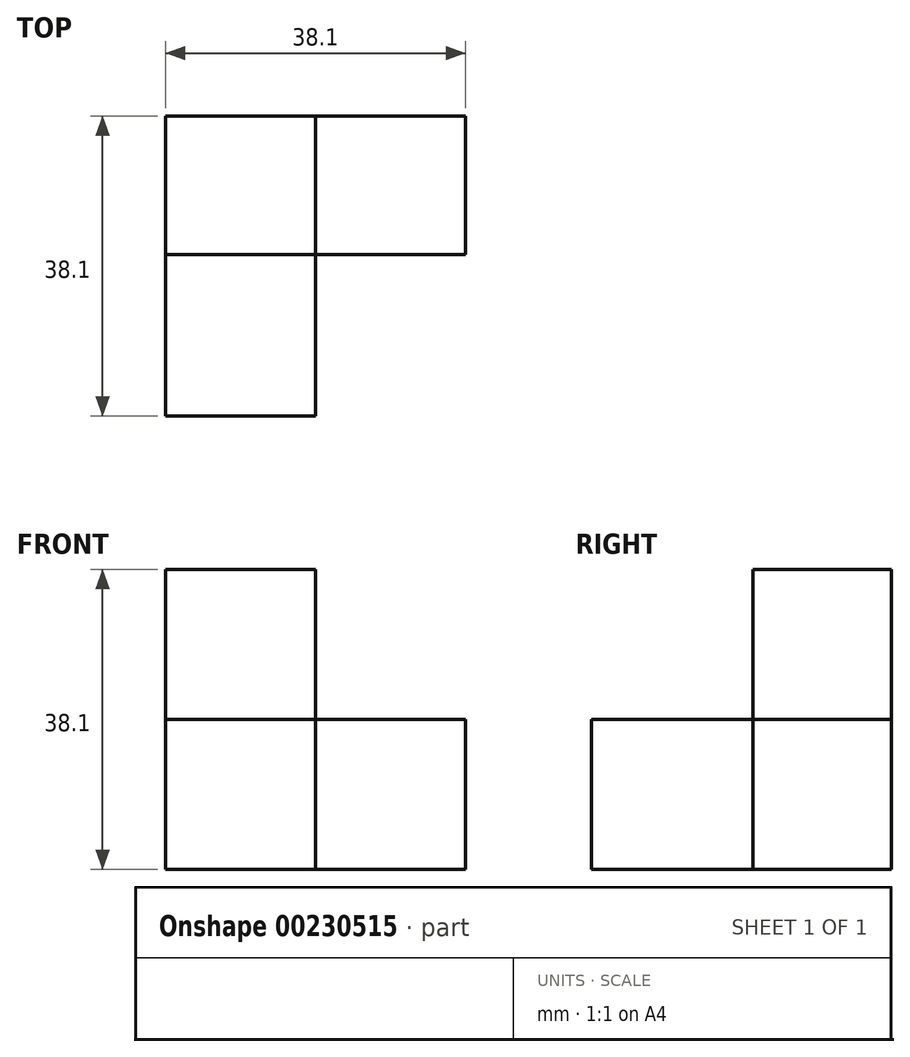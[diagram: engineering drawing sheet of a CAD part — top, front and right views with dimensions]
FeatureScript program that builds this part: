
annotation { "Feature Type Name" : "Feature", "Feature Type Description" : "" }
export const myFeature = defineFeature(function(context is Context, id is Id, definition is map)
    precondition{}
    {
        {
            var Q0;
            Q0=qCreatedBy(makeId("Top.planeOp"),FACE);
            var sketch = newSketch(context, id + "F0", { "sketchPlane" : qUnion([Q0])});
            skLineSegment(sketch, "E0.bottom", {"start": v(-44.26, -20.52) * mm, "end": v(-25.2, -20.52) * mm});
            skLineSegment(sketch, "E0.top", {"start": v(-44.26, 17.58) * mm, "end": v(-25.2, 17.58) * mm});
            skLineSegment(sketch, "E0.left", {"start": v(-44.26, -20.52) * mm, "end": v(-44.26, 17.58) * mm});
            skLineSegment(sketch, "E0.right", {"start": v(-25.2, -20.52) * mm, "end": v(-25.2, 17.58) * mm});
            skSolve(sketch);
        }
        {
            var Q0;
            Q0=makeQuery(id+"F0.imprint","IMPRINT",FACE,{"disambiguationData":[TD([[makeQuery(id+"F0.imprint","IMPRINT",EDGE,{"derivedFrom":sQuery(id+"F0.wireOp",EDGE,"E0.bottom")}),1.0]])]});
            extrude(context, id + "F1", {"entities" : qUnion([Q0]), "depth" : 19.05 * mm});
        }
        {
            var Q0;
            Q0=makeQuery(id+"F1.opExtrude","SWEPT_FACE",FACE,{"disambiguationData":[OSD([sQuery(id+"F0.wireOp",EDGE,"E0.right")])]});
            var sketch = newSketch(context, id + "F2", { "sketchPlane" : qUnion([Q0])});
            skLineSegment(sketch, "E1.bottom", {"start": v(17.58, 19.05) * mm, "end": v(0, 19.05) * mm});
            skLineSegment(sketch, "E1.top", {"start": v(17.58, 0) * mm, "end": v(0, 0) * mm});
            skLineSegment(sketch, "E1.left", {"start": v(17.58, 19.05) * mm, "end": v(17.58, 0) * mm});
            skLineSegment(sketch, "E1.right", {"start": v(0, 19.05) * mm, "end": v(0, 0) * mm});
            skSolve(sketch);
        }
        {
            var Q0;
            Q0 = qSketchRegion(id + "F2", true);
            extrude(context, id + "F3", {"entities" : qUnion([Q0]), "operationType" : NewBodyOperationType.ADD, "depth" : 19.05 * mm});
        }
        {
            var Q0;
            Q0=makeQuery(id+"F3.boolean.opBoolean","MERGE",FACE,{"derivedFrom":[makeQuery(id+"F1.opExtrude","CAP_FACE",FACE,{"disambiguationData":[OSD([sQuery(id+"F0.wireOp",EDGE,"E0.bottom"),sQuery(id+"F0.wireOp",EDGE,"E0.top"),sQuery(id+"F0.wireOp",EDGE,"E0.left"),sQuery(id+"F0.wireOp",EDGE,"E0.right")])],"isStart":false}),makeQuery(id+"F3.opExtrude","SWEPT_FACE",FACE,{"disambiguationData":[OSD([sQuery(id+"F2.wireOp",EDGE,"E1.bottom")])]})]});
            var sketch = newSketch(context, id + "F4", { "sketchPlane" : qUnion([Q0])});
            skLineSegment(sketch, "E2.bottom", {"start": v(-25.2, 0) * mm, "end": v(-44.26, 0) * mm});
            skLineSegment(sketch, "E2.top", {"start": v(-25.2, 17.58) * mm, "end": v(-44.26, 17.58) * mm});
            skLineSegment(sketch, "E2.left", {"start": v(-25.2, 0) * mm, "end": v(-25.2, 17.58) * mm});
            skLineSegment(sketch, "E2.right", {"start": v(-44.26, 0) * mm, "end": v(-44.26, 17.58) * mm});
            skSolve(sketch);
        }
        {
            var Q0;
            Q0=makeQuery(id+"F4.imprint","IMPRINT",FACE,{"disambiguationData":[TD([[makeQuery(id+"F4.imprint","IMPRINT",EDGE,{"derivedFrom":sQuery(id+"F4.wireOp",EDGE,"E2.bottom")}),-1.0]])]});
            extrude(context, id + "F5", {"entities" : qUnion([Q0]), "operationType" : NewBodyOperationType.ADD, "depth" : 19.05 * mm});
        }
    });
